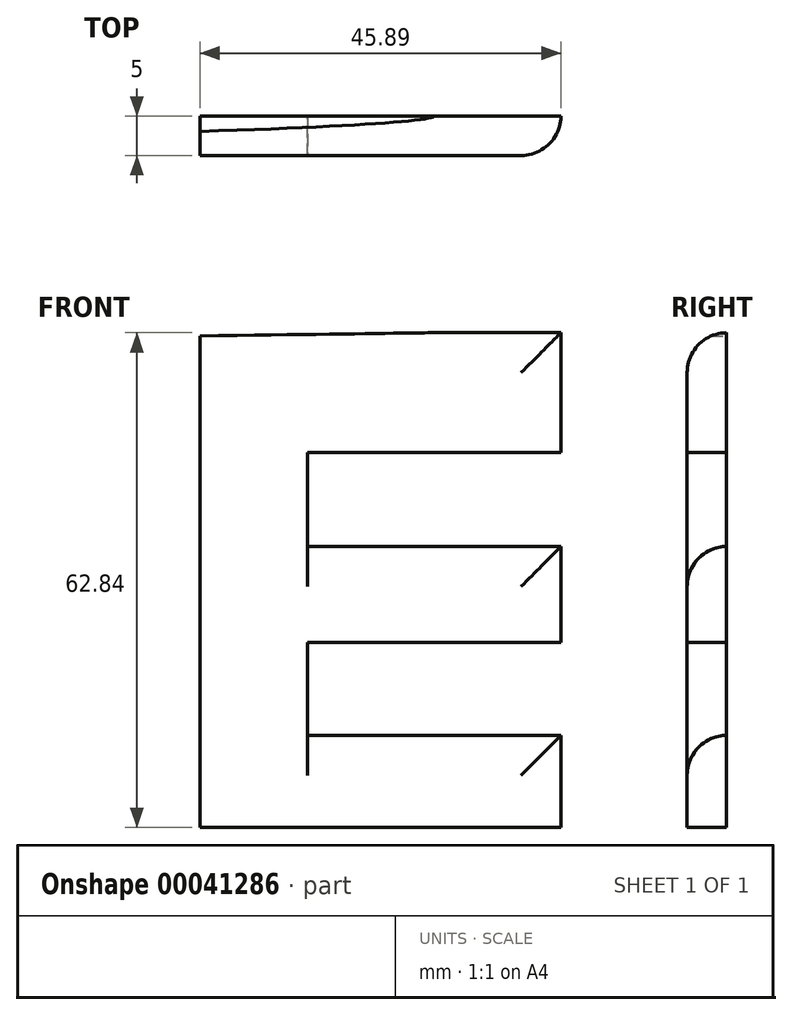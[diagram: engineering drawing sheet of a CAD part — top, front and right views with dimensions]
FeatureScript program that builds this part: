
annotation { "Feature Type Name" : "Feature", "Feature Type Description" : "" }
export const myFeature = defineFeature(function(context is Context, id is Id, definition is map)
    precondition{}
    {
        {
            var Q0;
            Q0=qCreatedBy(makeId("Front.planeOp"),FACE);
            var sketch = newSketch(context, id + "F0", { "sketchPlane" : qUnion([Q0])});
            skLineSegment(sketch, "E0", {"start": v(-47.98, 39.33) * mm, "end": v(-15.77, 39.33) * mm});
            skLineSegment(sketch, "E1", {"start": v(-15.77, 39.33) * mm, "end": v(-15.77, 24.1) * mm});
            skLineSegment(sketch, "E2", {"start": v(-15.77, 24.1) * mm, "end": v(-47.98, 24.1) * mm});
            skLineSegment(sketch, "E3", {"start": v(-47.98, 24.1) * mm, "end": v(-47.98, 12.17) * mm});
            skLineSegment(sketch, "E4", {"start": v(-47.98, 12.17) * mm, "end": v(-15.77, 12.17) * mm});
            skLineSegment(sketch, "E5", {"start": v(-15.77, 12.17) * mm, "end": v(-15.77, 0) * mm});
            skLineSegment(sketch, "E6", {"start": v(-15.77, 0) * mm, "end": v(-47.98, 0) * mm});
            skLineSegment(sketch, "E7", {"start": v(-47.98, 0) * mm, "end": v(-47.98, -11.82) * mm});
            skLineSegment(sketch, "E8", {"start": v(-47.98, -11.82) * mm, "end": v(-15.77, -11.82) * mm});
            skLineSegment(sketch, "E9", {"start": v(-15.77, -11.82) * mm, "end": v(-15.77, -23.5) * mm});
            skLineSegment(sketch, "E10", {"start": v(-15.77, -23.5) * mm, "end": v(-61.66, -23.5) * mm});
            skLineSegment(sketch, "E11", {"start": v(-61.66, -23.5) * mm, "end": v(-61.66, 38.91) * mm});
            skLineSegment(sketch, "E12", {"start": v(-61.66, 38.91) * mm, "end": v(-31.87, 39.33) * mm});
            skSolve(sketch);
        }
        {
            var Q0;
            {var subQ1=sQuery(id+"F0.wireOp",EDGE,"E1");Q0=makeQuery(id+"F0.imprint","IMPRINT",FACE,{"disambiguationData":[TD([[makeQuery(id+"F0.imprint","IMPRINT",EDGE,{"derivedFrom":subQ1}),-1.0]])]});}
            extrude(context, id + "F1", {"entities" : qUnion([Q0]), "depth" : 5 * mm});
        }
        {
            var Q0;
            Q0=makeQuery(id+"F1.opExtrude","CAP_EDGE",EDGE,{"disambiguationData":[OSD([sQuery(id+"F0.wireOp",EDGE,"E1")])],"isStart":false});
            fillet(context, id + "F2", {"entities" : qUnion([Q0]), "radius" : 5.08 * mm, "tangentPropagation" : true, "allowEdgeOverflow" : false});
        }
        {
            var Q0;
            Q0=makeQuery(id+"F1.opExtrude","CAP_EDGE",EDGE,{"disambiguationData":[OSD([sQuery(id+"F0.wireOp",EDGE,"E5")])],"isStart":false});
            fillet(context, id + "F3", {"entities" : qUnion([Q0]), "radius" : 5.08 * mm, "tangentPropagation" : true, "allowEdgeOverflow" : false});
        }
        {
            var Q0;
            Q0=makeQuery(id+"F1.opExtrude","CAP_EDGE",EDGE,{"disambiguationData":[OSD([sQuery(id+"F0.wireOp",EDGE,"E9")])],"isStart":false});
            fillet(context, id + "F5", {"entities" : qUnion([Q0]), "radius" : 5.08 * mm, "tangentPropagation" : true, "allowEdgeOverflow" : false});
        }
        {
            var Q0;
            Q0=makeQuery(id+"F2.opFillet","BLEND_EDGE",EDGE,{"blendedFrom":[makeQuery(id+"F1.opExtrude","CAP_EDGE",EDGE,{"disambiguationData":[OSD([sQuery(id+"F0.wireOp",EDGE,"E1")])],"isStart":false}),makeQuery(id+"F1.opExtrude","SWEPT_FACE",FACE,{"disambiguationData":[OSD([sQuery(id+"F0.wireOp",EDGE,"E0")])]})],"blendedInto":[makeQuery(id+"F1.opExtrude","SWEPT_FACE",FACE,{"disambiguationData":[OSD([sQuery(id+"F0.wireOp",EDGE,"E0")])]})]});
            fillet(context, id + "F6", {"entities" : qUnion([Q0]), "radius" : 5.08 * mm, "tangentPropagation" : true, "allowEdgeOverflow" : false});
        }
        {
            var Q0;
            Q0=makeQuery(id+"F1.opExtrude","CAP_EDGE",EDGE,{"disambiguationData":[OSD([sQuery(id+"F0.wireOp",EDGE,"E4")])],"isStart":false});
            fillet(context, id + "F4", {"entities" : qUnion([Q0]), "radius" : 5.08 * mm, "tangentPropagation" : true, "allowEdgeOverflow" : false});
        }
        {
            var Q0;
            Q0=makeQuery(id+"F1.opExtrude","CAP_EDGE",EDGE,{"disambiguationData":[OSD([sQuery(id+"F0.wireOp",EDGE,"E8")])],"isStart":false});
            fillet(context, id + "F7", {"entities" : qUnion([Q0]), "radius" : 5.08 * mm, "tangentPropagation" : true, "allowEdgeOverflow" : false});
        }
    });
